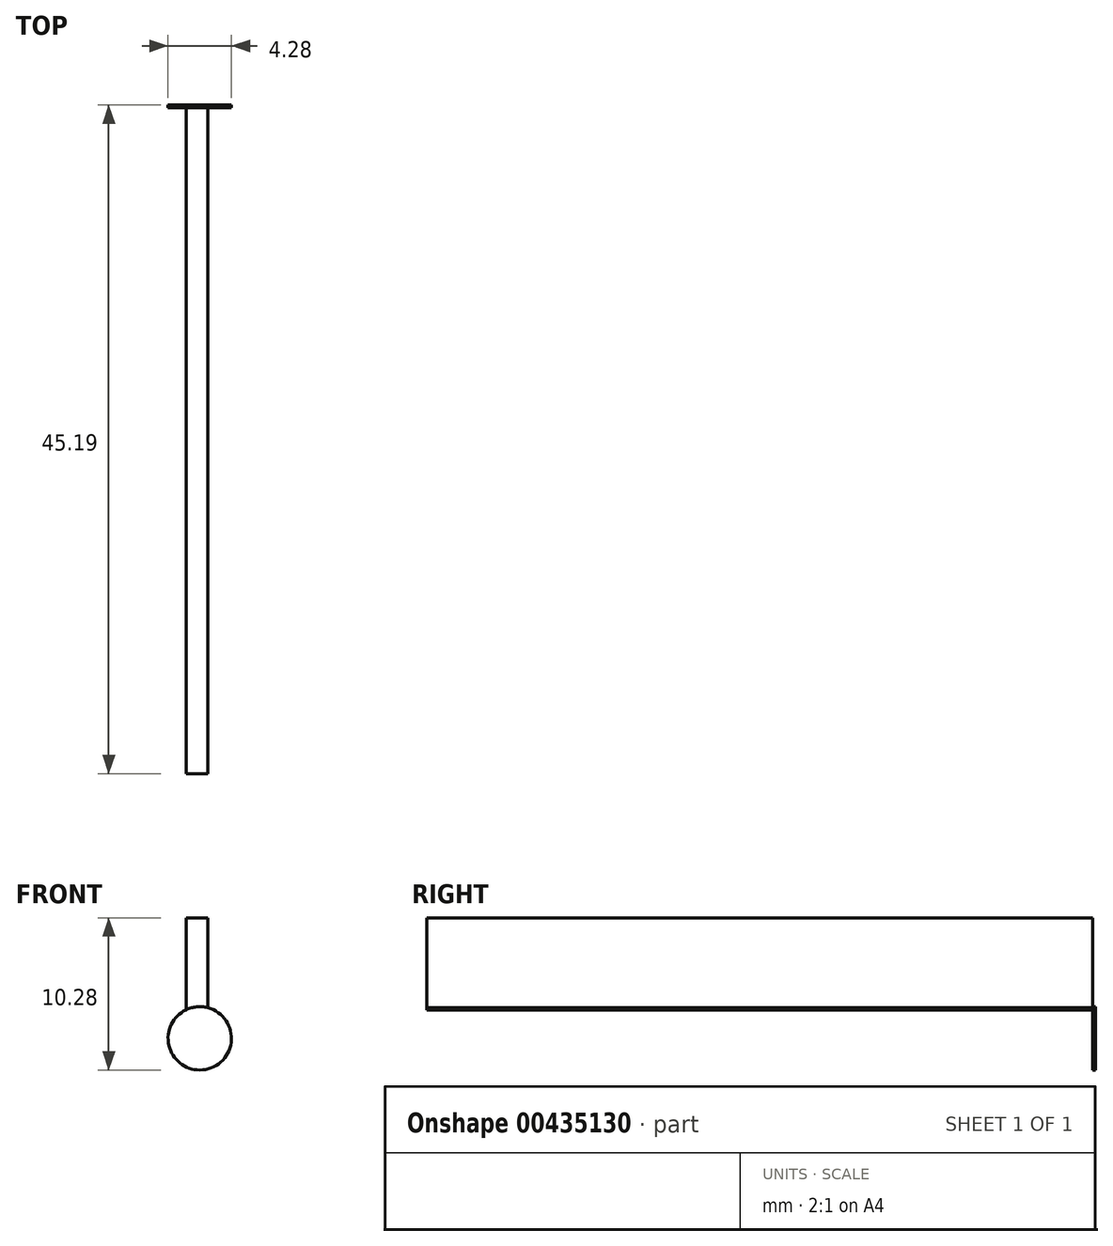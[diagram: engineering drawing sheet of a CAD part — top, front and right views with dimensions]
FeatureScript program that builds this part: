
annotation { "Feature Type Name" : "Feature", "Feature Type Description" : "" }
export const myFeature = defineFeature(function(context is Context, id is Id, definition is map)
    precondition{}
    {
        {
            var Q0;
            Q0=qCreatedBy(makeId("Front.planeOp"),FACE);
            var sketch = newSketch(context, id + "F0", { "sketchPlane" : qUnion([Q0])});
            skCircle(sketch, "E0", {"center": v(-39.4, 7.74) * mm, "radius": 2.14 * mm});
            skCircle(sketch, "E1", {"center": v(-39.4, 7.74) * mm, "radius": 0.34 * mm});
            skSolve(sketch);
        }
        {
            var Q0;
            Q0=makeQuery(id+"F0.imprint","IMPRINT",FACE,{"disambiguationData":[TD([[makeQuery(id+"F0.imprint","IMPRINT",EDGE,{"derivedFrom":sQuery(id+"F0.wireOp",EDGE,"E0")}),1.0]])]});
            var Q1;
            Q1=makeQuery(id+"F0.imprint","IMPRINT",FACE,{"disambiguationData":[TD([[makeQuery(id+"F0.imprint","IMPRINT",EDGE,{"derivedFrom":sQuery(id+"F0.wireOp",EDGE,"E1")}),1.0]])]});
            extrude(context, id + "F1", {"entities" : qUnion([Q0, Q1]), "oppositeDirection" : true, "depth" : 0.19 * mm});
        }
        {
            var Q0;
            Q0=sQuery(id+"F0.wireOp",EDGE,"E1");
            extrude(context, id + "F2", {"bodyType" : ToolBodyType.SURFACE, "surfaceEntities" : qUnion([Q0]), "oppositeDirection" : true, "depth" : 0.45 * mm});
        }
        {
            var Q0;
            Q0=makeQuery(id+"F1.opExtrude","CAP_FACE",FACE,{"disambiguationData":[OSD([sQuery(id+"F0.wireOp",EDGE,"E0")])],"isStart":true});
            var sketch = newSketch(context, id + "F3", { "sketchPlane" : qUnion([Q0])});
            skLineSegment(sketch, "E2", {"start": v(-40.33, 9.66) * mm, "end": v(-40.33, 15.88) * mm});
            skLineSegment(sketch, "E3", {"start": v(-40.33, 15.88) * mm, "end": v(-38.86, 15.88) * mm});
            skLineSegment(sketch, "E4", {"start": v(-38.86, 15.88) * mm, "end": v(-38.86, 9.8) * mm});
            skSolve(sketch);
        }
        {
            var Q0;
            {var subQ0=sQuery(id+"F3.wireOp",EDGE,"E2");Q0=makeQuery(id+"F3.imprint","IMPRINT",FACE,{"disambiguationData":[TD([[makeQuery(id+"F3.imprint","IMPRINT",EDGE,{"derivedFrom":subQ0}),-1.0]])]});}
            extrude(context, id + "F4", {"entities" : qUnion([Q0]), "depth" : 45 * mm});
        }
        {
            var Q0;
            Q0=makeQuery(id+"F4.opExtrude","CAP_FACE",FACE,{"disambiguationData":[OSD([sQuery(id+"F0.wireOp",EDGE,"E0"),sQuery(id+"F3.wireOp",EDGE,"E2"),sQuery(id+"F3.wireOp",EDGE,"E3"),sQuery(id+"F3.wireOp",EDGE,"E4")])],"isStart":false});
            var sketch = newSketch(context, id + "F5", { "sketchPlane" : qUnion([Q0])});
            skCircle(sketch, "E5", {"center": v(-39.6, 15.88) * mm, "radius": 0.8 * mm});
            skSolve(sketch);
        }
        {
            var Q0;
            Q0=sQuery(id+"F5.wireOp",EDGE,"E5");
            extrude(context, id + "F6", {"bodyType" : ToolBodyType.SURFACE, "surfaceEntities" : qUnion([Q0]), "depth" : 45 * mm});
        }
    });
